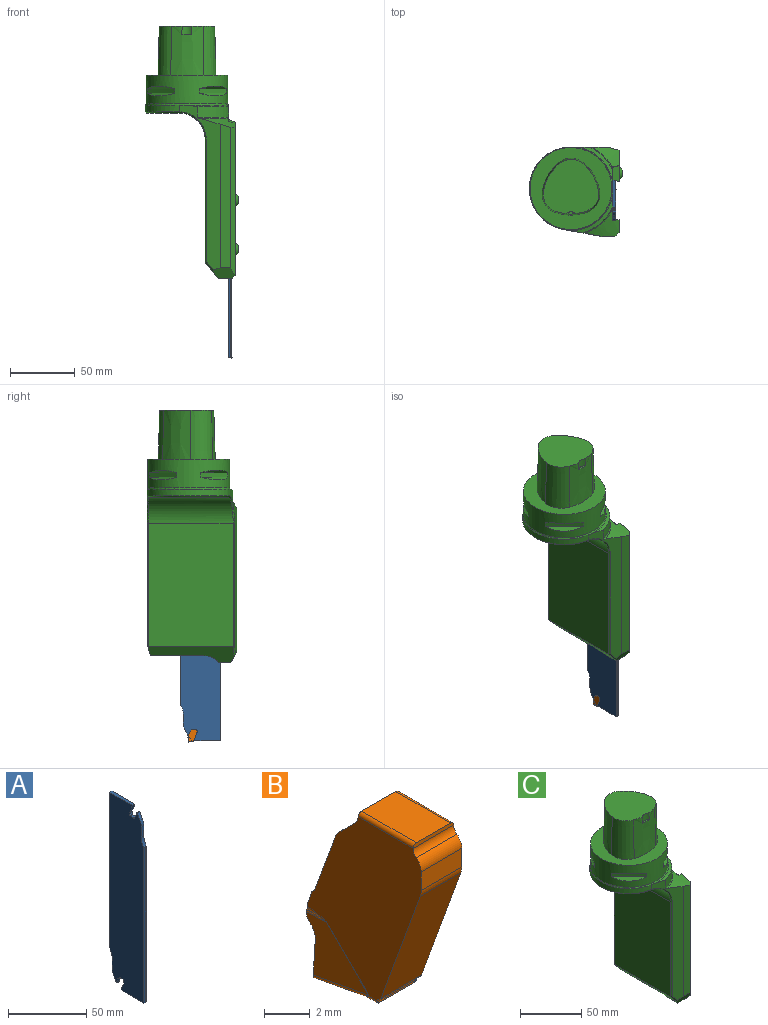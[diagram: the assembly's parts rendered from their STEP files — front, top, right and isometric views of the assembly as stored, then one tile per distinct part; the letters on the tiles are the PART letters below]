
ASSEMBLY  parts=3 mates=3
PART A: 58 faces, bbox 7.9x35x152.9 mm
  f0: plane 149.15x30.64mm, normal (-1,0,0), area 4314.1mm2, adj f1,f11,f12,f13,f14,f15,f16,f17
  f1: plane 2.35x0.99mm, normal (0,-1,0), area 2.3mm2, adj f0,f2,f11,f53
  f2: plane 149.15x30.64mm, normal (1,0,0), area 4314.1mm2, adj f1,f3,f4,f5,f7,f8,f9,f11
  f3: plane 121.39x1.19mm, normal (0.26,0.97,0), area 147.4mm2, adj f2,f49,f50,f51
  f4: cylinder r=0.2mm len=0.91mm, axis (-1,0,0), area 0mm2, adj f2,f41,f46
  f5: cylinder r=0.2mm len=3.37mm, axis (0,-1,0), area 0.5mm2, adj f2,f6,f34,f36
  f6: plane 3.37x2.1mm, normal (0,0,-1), area 7.1mm2, adj f5,f34,f35,f36
  f7: plane 121.39x1.19mm, normal (0.26,-0.97,0), area 147.4mm2, adj f2,f26,f27,f28
  f8: cylinder r=0.2mm len=0.91mm, axis (-1,0,0), area 0mm2, adj f2,f20,f23
  f9: cylinder r=0.2mm len=3.37mm, axis (0,1,0), area 0.5mm2, adj f2,f10,f13,f15
  f10: plane 3.37x2.1mm, normal (0,0,1), area 7.1mm2, adj f9,f13,f14,f15
  f11: cylinder r=0.75mm len=2.35mm, axis (-1,0,0), area 1.6mm2, adj f0,f1,f2,f12
  f12: cylinder r=0.5mm len=2.35mm, axis (-1,0,0), area 1.1mm2, adj f0,f2,f11,f13
  f13: plane 2.35x0.2mm, normal (0,-1,0), area 0.5mm2, adj f0,f2,f9,f10,f12,f14
  f14: cylinder r=0.2mm len=3.37mm, axis (0,-1,0), area 0.5mm2, adj f0,f10,f13,f15
  f15: plane 2.35x0.1mm, normal (0,1,0), area 0.2mm2, adj f0,f2,f9,f10,f14,f16
  f16: cylinder r=0.8mm len=2.35mm, axis (1,0,0), area 1.5mm2, adj f0,f2,f15,f17
  f17: plane 2.35x0.96mm, normal (0,0.71,0.71), area 3.2mm2, adj f0,f2,f16,f18
  f18: cylinder r=1mm len=2.35mm, axis (-1,0,0), area 1mm2, adj f0,f2,f17,f19
  f19: plane 3.38x2.35mm, normal (0,0.94,0.34), area 8.5mm2, adj f0,f2,f18,f20
  f20: cylinder r=0.4mm len=2.35mm, axis (-1,0,0), area 0.5mm2, adj f0,f2,f8,f19,f21,f22
  f21: bspline ~0.53x0.1mm, area 0mm2, adj f20,f23
  f22: cylinder r=0.2mm len=0.91mm, axis (-1,0,0), area 0mm2, adj f0,f20,f23
  f23: plane 4.37x2.56mm, normal (0,-0.87,0.5), area 11.6mm2, adj f0,f2,f8,f21,f22,f24
  f24: cylinder r=10mm len=5mm, axis (1,0,0), area 12.3mm2, adj f0,f2,f23,f25
  f25: plane 7.69x2.35mm, normal (0,-1,0), area 18.1mm2, adj f0,f2,f24,f26
  f26: cylinder r=13mm len=7.68mm, axis (-1,0,0), area 18.7mm2, adj f0,f2,f7,f25,f27
  f27: plane 121.39x1.19mm, normal (-0.26,-0.97,0), area 147.4mm2, adj f0,f7,f26,f28
  f28: plane 20.75x2.35mm, normal (0,0,-1), area 48.4mm2, adj f0,f2,f7,f27,f29
  f29: plane 6.61x2.41mm, normal (0,0.94,0.34), area 16.5mm2, adj f0,f2,f28,f30
  f30: cylinder r=1mm len=2.35mm, axis (1,0,0), area 0.8mm2, adj f0,f2,f29,f31
  f31: plane 2.35x0.99mm, normal (0,1,0), area 2.3mm2, adj f0,f2,f30,f32
  f32: cylinder r=0.75mm len=2.35mm, axis (-1,0,0), area 1.6mm2, adj f0,f2,f31,f33
  f33: cylinder r=0.5mm len=2.35mm, axis (-1,0,0), area 1.1mm2, adj f0,f2,f32,f34
  f34: plane 2.35x0.2mm, normal (0,1,0), area 0.5mm2, adj f0,f2,f5,f6,f33,f35
  f35: cylinder r=0.2mm len=3.37mm, axis (0,1,0), area 0.5mm2, adj f0,f6,f34,f36
  f36: plane 2.35x0.1mm, normal (0,-1,0), area 0.2mm2, adj f0,f2,f5,f6,f35,f37
  f37: cylinder r=0.8mm len=2.35mm, axis (1,0,0), area 1.5mm2, adj f0,f2,f36,f38
  f38: plane 2.35x0.96mm, normal (0,-0.71,-0.71), area 3.2mm2, adj f0,f2,f37,f39
  f39: cylinder r=1mm len=2.35mm, axis (-1,0,0), area 1mm2, adj f0,f2,f38,f40
  f40: plane 3.38x2.35mm, normal (0,-0.94,-0.34), area 8.5mm2, adj f0,f2,f39,f41
  f41: cylinder r=0.4mm len=2.35mm, axis (-1,0,0), area 0.5mm2, adj f0,f2,f4,f40,f42,f45
  f42: bspline ~0.53x0.1mm, area 0mm2, adj f41,f43,f44,f46
  f43: plane 5.57x3.98mm, normal (0,0.87,-0.5), area -0.2mm2, adj f42
  f44: plane 6x3.91mm, normal (0,0.87,-0.5), area 0.4mm2, adj f42
  f45: cylinder r=0.2mm len=0.91mm, axis (-1,0,0), area 0mm2, adj f0,f41,f46
  f46: plane 4.82x3.01mm, normal (0,0.87,-0.5), area 11.6mm2, adj f0,f2,f4,f42,f45,f47
  f47: cylinder r=10mm len=5mm, axis (1,0,0), area 12.3mm2, adj f0,f2,f46,f48
  f48: plane 7.69x2.35mm, normal (0,1,0), area 18.1mm2, adj f0,f2,f47,f49
  f49: cylinder r=13mm len=7.68mm, axis (-1,0,0), area 18.7mm2, adj f0,f2,f3,f48,f50
  f50: plane 121.39x1.19mm, normal (-0.26,0.97,0), area 147.4mm2, adj f0,f3,f49,f51
  f51: plane 20.75x2.35mm, normal (0,0,1), area 48.4mm2, adj f0,f2,f3,f50,f52
  f52: plane 6.61x2.41mm, normal (0,-0.94,-0.34), area 16.5mm2, adj f0,f2,f51,f53
  f53: cylinder r=1mm len=2.35mm, axis (1,0,0), area 0.8mm2, adj f0,f1,f2,f52
  f54: bspline ~0.53x0.1mm, area 0mm2, adj f55
  f55: sphere r=0.2mm, area 0.3mm2, adj f54
  f56: bspline ~0.53x0.1mm, area 0mm2, adj f57
  f57: sphere r=0.2mm, area 0mm2, adj f56
PART B: 78 faces, bbox 3x7x10 mm
  f0: plane 9.25x7mm, normal (1,0,0), area 40.2mm2, adj f3,f14,f17,f19,f20,f21,f30,f31
  f1: plane 9.25x7mm, normal (-1,0,0), area 40.2mm2, adj f4,f15,f18,f27,f28,f29,f30,f31
  f2: plane 3.37x2.1mm, normal (0,0,1), area 7.1mm2, adj f3,f4,f38,f57
  f3: cylinder r=0.2mm len=3.38mm, axis (0,-1,0), area 1.1mm2, adj f0,f2,f38,f49,f57
  f4: cylinder r=0.2mm len=3.38mm, axis (0,1,0), area 1.1mm2, adj f1,f2,f38,f49,f57
  f5: plane 3.77x3.02mm, normal (-1,-0.07,0.07), area 5.8mm2, adj f9,f13,f28,f58,f59,f60,f61
  f6: plane 0.41x0.06mm, normal (-0.86,-0.07,0.5), area 0mm2, adj f13,f15,f51
  f7: plane 3.77x3.02mm, normal (1,-0.07,0.07), area 5.8mm2, adj f10,f12,f20,f55,f56,f58,f61
  f8: plane 0.41x0.06mm, normal (0.86,-0.07,0.5), area 0mm2, adj f12,f14,f50
  f9: cylinder r=0.2mm len=3.2mm, axis (0.08,-0.99,0.12), area 1mm2, adj f5,f11,f26,f27,f61
  f10: cylinder r=0.2mm len=3.18mm, axis (-0.08,-0.99,0.12), area 1mm2, adj f7,f11,f21,f22,f61
  f11: plane 2.85x2.6mm, normal (0,-0.12,-0.99), area 6.8mm2, adj f9,f10,f23,f24,f25,f61
  f12: cylinder r=0.2mm len=1.18mm, axis (-0.07,-1,-0.02), area 0.1mm2, adj f7,f8,f19,f50,f56
  f13: cylinder r=0.2mm len=1.18mm, axis (0.07,-1,-0.02), area 0.1mm2, adj f5,f6,f29,f51,f60
  f14: cylinder r=0.2mm len=0.44mm, axis (0,0.99,0.14), area 0mm2, adj f0,f8,f19,f50
  f15: cylinder r=0.2mm len=0.44mm, axis (0,-0.99,-0.14), area 0mm2, adj f1,f6,f29,f51
  f16: plane 2.1x0.78mm, normal (0,0,-1), area 1.6mm2, adj f17,f18,f24,f39
  f17: cylinder r=0.2mm len=0.8mm, axis (0,1,0), area 0.2mm2, adj f0,f16,f22,f23,f37,f39
  f18: cylinder r=0.2mm len=0.8mm, axis (0,-1,0), area 0.2mm2, adj f1,f16,f25,f26,f37,f39
  f19: bspline ~0.78x0.2mm, area 0.1mm2, adj f0,f12,f14,f20
  f20: cylinder r=0.2mm len=2.6mm, axis (0,0.71,0.71), area 0.1mm2, adj f0,f7,f19,f21
  f21: plane 0.1x0.08mm, normal (1,-0.04,-0.01), area 0mm2, adj f0,f10,f20,f22
  f22: bspline ~0.32x0.22mm, area 0mm2, adj f10,f17,f21,f23
  f23: bspline ~0.03x0.03mm, area 0mm2, adj f11,f17,f22,f24
  f24: cylinder r=0.2mm len=2.1mm, axis (1,0,0), area 0.1mm2, adj f11,f16,f23,f25
  f25: cylinder r=0.13mm len=0.04mm, axis (-0.98,0.18,0.01), area 0mm2, adj f11,f18,f24,f26
  f26: bspline ~0.32x0.22mm, area 0mm2, adj f9,f18,f25,f27
  f27: plane 0.07x0.05mm, normal (-1,-0.04,-0.01), area 0mm2, adj f1,f9,f26,f28
  f28: cylinder r=0.2mm len=2.6mm, axis (0,-0.71,-0.71), area 0.1mm2, adj f1,f5,f27,f29
  f29: bspline ~0.78x0.2mm, area 0.1mm2, adj f1,f13,f15,f28
  f30: cylinder r=0.75mm len=2.5mm, axis (-1,0,0), area 1.7mm2, adj f0,f1,f31,f32
  f31: plane 2.5x0.99mm, normal (0,-1,0), area 2.5mm2, adj f0,f1,f30,f35
  f32: cylinder r=0.5mm len=2.5mm, axis (-1,0,0), area 1.2mm2, adj f0,f1,f30,f38
  f33: plane 6.66x2.5mm, normal (0,-0.94,-0.34), area 17.7mm2, adj f0,f1,f35,f36
  f34: plane 2.5x0.08mm, normal (0,-0.5,-0.87), area 0.2mm2, adj f0,f1,f36,f37
  f35: cylinder r=1mm len=2.5mm, axis (1,0,0), area 0.9mm2, adj f0,f1,f31,f33
  f36: cylinder r=0.1mm len=2.5mm, axis (-1,0,0), area 0.2mm2, adj f0,f1,f33,f34
  f37: cylinder r=0.3mm len=2.5mm, axis (-1,0,0), area 0.8mm2, adj f0,f1,f17,f18,f34,f39
  f38: plane 2.5x0.2mm, normal (0,-1,0), area 0.5mm2, adj f2,f3,f4,f32
  f39: plane 2.45x0.1mm, normal (0,-1,0), area 0.2mm2, adj f16,f17,f18,f37
  f40: cylinder r=0.2mm len=0.99mm, axis (-1,0,0), area 0.1mm2, adj f0,f42,f44,f77
  f41: cylinder r=0.2mm len=0.66mm, axis (1,0,0), area 0mm2, adj f0,f42,f50,f73
  f42: plane 0.99x0.69mm, normal (0,0.94,0.34), area 0.6mm2, adj f0,f40,f41,f75
  f43: cylinder r=0.2mm len=1.01mm, axis (-1,0,0), area 0.1mm2, adj f1,f44,f48,f74,f76
  f44: cylinder r=0.4mm len=2.5mm, axis (-1,0,0), area 0.6mm2, adj f0,f1,f40,f43,f45,f76
  f45: plane 3.38x2.5mm, normal (0,0.94,0.34), area 9mm2, adj f0,f1,f44,f47
  f46: plane 2.5x0.96mm, normal (0,0.71,0.71), area 3.4mm2, adj f0,f1,f47,f49
  f47: cylinder r=1mm len=2.5mm, axis (-1,0,0), area 1.1mm2, adj f0,f1,f45,f46
  f48: plane 0.99x0.72mm, normal (0,0.94,0.34), area 0.6mm2, adj f1,f43,f51,f74
  f49: cylinder r=0.8mm len=2.5mm, axis (1,0,0), area 1.6mm2, adj f0,f1,f3,f4,f46,f57
  f50: plane 0.74x0.37mm, normal (0,1,0), area 0.2mm2, adj f0,f8,f12,f14,f41,f56,f69,f71
  f51: plane 0.74x0.41mm, normal (0,1,0), area 0.3mm2, adj f1,f6,f13,f15,f48,f60,f70,f72
  f52: cylinder r=0.45mm len=1.99mm, axis (0,0.12,0.99), area 1.5mm2, adj f53,f54,f62,f63,f64,f65,f66,f71
  f53: plane 0.38x0.05mm, normal (-0.93,0.37,-0.05), area 0mm2, adj f52,f67,f69
  f54: plane 0.38x0.05mm, normal (0.93,0.37,-0.05), area 0mm2, adj f52,f68,f70
  f55: plane 0.85x0.16mm, normal (0,0.71,-0.71), area 0.2mm2, adj f7,f56,f58,f63
  f56: cylinder r=0.5mm len=0.76mm, axis (-1,0,0), area 0.3mm2, adj f7,f12,f50,f55,f65,f67
  f57: plane 2.45x0.1mm, normal (0,1,0), area 0.2mm2, adj f2,f3,f4,f49
  f58: cylinder r=1mm len=2.75mm, axis (-1,0,0), area 1.8mm2, adj f5,f7,f55,f59,f61,f62
  f59: plane 0.85x0.16mm, normal (0,0.71,-0.71), area 0.2mm2, adj f5,f58,f60,f64
  f60: cylinder r=0.5mm len=0.76mm, axis (-1,0,0), area 0.3mm2, adj f5,f13,f51,f59,f66,f68
  f61: plane 3.02x2.02mm, normal (0,1,0), area 5.8mm2, adj f5,f7,f9,f10,f11,f58
  f62: bspline ~1x0.52mm, area 0.2mm2, adj f52,f58,f63,f64
  f63: bspline ~0.29x0.24mm, area 0.1mm2, adj f52,f55,f62,f65
  f64: bspline ~0.29x0.24mm, area 0.1mm2, adj f52,f59,f62,f66
  f65: bspline ~0.2x0.18mm, area 0mm2, adj f52,f56,f63,f67
  f66: bspline ~0.2x0.18mm, area 0mm2, adj f52,f60,f64,f68
  f67: bspline ~0.27x0.2mm, area 0.1mm2, adj f53,f56,f65,f69
  f68: bspline ~0.27x0.2mm, area 0.1mm2, adj f54,f60,f66,f70
  f69: cylinder r=0.2mm len=0.23mm, axis (0.05,0,-1), area 0.1mm2, adj f50,f53,f67,f71
  f70: cylinder r=0.2mm len=0.23mm, axis (0.05,0,1), area 0.1mm2, adj f51,f54,f68,f72
  f71: cylinder r=0.2mm len=0.19mm, axis (-0.05,0,1), area 0mm2, adj f50,f52,f69,f73
  f72: cylinder r=0.2mm len=0.2mm, axis (0.06,0,1), area 0mm2, adj f51,f52,f70,f74
  f73: sphere r=0.2mm, area 0mm2, adj f41,f71,f75
  f74: bspline ~0.81x0.43mm, area 0.1mm2, adj f43,f48,f51,f52,f72,f76
  f75: bspline ~0.77x0.41mm, area 0.1mm2, adj f42,f52,f73,f77
  f76: bspline ~0.56x0.23mm, area 0.1mm2, adj f43,f44,f52,f74,f77
  f77: sphere r=0.2mm, area 0mm2, adj f40,f75,f76
PART C: 103 faces, bbox 80.9x91.1x194.7 mm
  f0: plane 3.16x0.1mm, normal (-1,0,0), area 0.3mm2, adj f1,f19,f41,f102
  f1: plane 3.51x0.7mm, normal (0,0,-1), area 2.4mm2, adj f0,f3,f41,f102
  f2: plane 3.16x0.1mm, normal (1,0,0), area 0.3mm2, adj f19,f40,f42,f102
  f3: plane 3.16x0.1mm, normal (1,0,0), area 0.3mm2, adj f1,f19,f41,f102
  f4: plane 76.42x8.84mm, normal (1,0,0), area 666.9mm2, adj f19,f21,f23,f24
  f5: plane 117.48x10.61mm, normal (1,0,0), area 1151.5mm2, adj f10,f22,f27,f36,f37
  f6: plane 133.26x39.63mm, normal (1,0,0), area 4060.6mm2, adj f10,f11,f12,f13,f14,f15,f16,f17
  f7: plane 114.13x11.55mm, normal (1,0,0), area 1288mm2, adj f11,f21,f23,f25,f43,f53
  f8: plane 10.93x9.38mm, normal (0,0,-1), area 97.4mm2, adj f20,f26,f27,f28,f32,f36,f37
  f9: plane 110.77x8.49mm, normal (0,-1,0), area 881.7mm2, adj f10,f22,f29,f36
  f10: cone r=35mm half-angle=65deg, axis (0,0,-1), area 269.8mm2, adj f5,f6,f9,f17,f22,f26,f27,f28
  f11: cone r=35mm half-angle=65deg, axis (0,0,-1), area 181.3mm2, adj f6,f7,f18,f25,f30,f38,f43
  f12: cone r=50mm half-angle=75deg, axis (0,0,-1), area 106.5mm2, adj f6,f14,f15,f29
  f13: cone r=50mm half-angle=75deg, axis (0,0,-1), area 90.6mm2, adj f6,f14,f16,f30
  f14: torus R=32.7mm, axis (0,0,1), area 267.6mm2, adj f6,f12,f13,f29,f30,f31,f54
  f15: cylinder r=35mm len=23.59mm, axis (0,0,1), area 267.2mm2, adj f6,f12,f17,f29
  f16: cylinder r=35mm len=17.82mm, axis (0,0,1), area 216mm2, adj f6,f13,f18,f30
  f17: torus R=36.2mm, axis (0,0,1), area 41.7mm2, adj f6,f10,f15,f29
  f18: torus R=36.2mm, axis (0,0,1), area 33.3mm2, adj f6,f11,f16,f30
  f19: plane 40.97x16.13mm, normal (0,0,-1), area 446.2mm2, adj f0,f2,f3,f4,f6,f20,f23,f24
  f20: cylinder r=16mm len=12.13mm, axis (1,0,0), area 139.1mm2, adj f6,f8,f19,f26,f32
  f21: cone r=6.94mm half-angle=15deg, axis (1,0,0), area 80mm2, adj f4,f6,f7,f23,f24,f25,f38
  f22: cylinder r=50mm len=113.84mm, axis (0,0,1), area 528.8mm2, adj f5,f9,f10,f36
  f23: plane 72x9.4mm, normal (0.26,-0.97,0), area 209.9mm2, adj f4,f7,f19,f21,f53,f80,f81,f84
  f24: plane 72x4.4mm, normal (0.26,0.97,0), area 328mm2, adj f4,f6,f19,f21
  f25: plane 43.93x4.76mm, normal (0.26,-0.97,0), area 207.8mm2, adj f7,f11,f21,f38
  f26: plane 121.07x1.29mm, normal (0.97,-0.26,0), area 160.1mm2, adj f6,f8,f10,f20,f28
  f27: plane 120.34x4.51mm, normal (-0.26,0.97,0), area 537.8mm2, adj f5,f8,f10,f28,f37
  f28: cylinder r=0.8mm len=120.84mm, axis (0,0,1), area 201.9mm2, adj f8,f10,f26,f27
  f29: plane 127.32x31.78mm, normal (-0.17,-0.98,0), area 1341.9mm2, adj f9,f10,f12,f14,f15,f17,f31,f36
  f30: plane 119.7x28.67mm, normal (0,1,0), area 1550.1mm2, adj f11,f13,f14,f16,f18,f31,f43,f46
  f31: cylinder r=32mm len=63.51mm, axis (0,0,1), area 479.9mm2, adj f14,f29,f30,f47,f49,f50
  f32: plane 66.4x12mm, normal (-0.77,0,-0.64), area 687.9mm2, adj f8,f19,f20,f35,f36,f46,f51,f52
  f33: cylinder r=20mm len=65.12mm, axis (0,1,0), area 2001.9mm2, adj f34,f35,f45,f47,f48,f50
  f34: plane 60.83x25mm, normal (0,0,-1), area 1139.9mm2, adj f33,f49
  f35: plane 95x65.12mm, normal (-1,0,0), area 6186.7mm2, adj f32,f33,f44,f46,f51
  f36: plane 16.95x8.14mm, normal (0,-0.87,-0.5), area 126.5mm2, adj f5,f8,f9,f22,f29,f32,f37,f51
  f37: plane 9.88x2mm, normal (0.71,0,-0.71), area 25.5mm2, adj f5,f8,f27,f36
  f38: cylinder r=0.4mm len=44.07mm, axis (0,0,-1), area 22.8mm2, adj f6,f11,f21,f25
  f39: plane 3.16x0.1mm, normal (-1,0,0), area 0.3mm2, adj f19,f40,f42,f102
  f40: plane 3.51x0.7mm, normal (0,0,-1), area 2.4mm2, adj f2,f39,f42,f102
  f41: cylinder r=0.35mm len=0.7mm, axis (0,0,-1), area 0.1mm2, adj f0,f1,f3,f19
  f42: cylinder r=0.35mm len=0.7mm, axis (0,0,-1), area 0.1mm2, adj f2,f19,f39,f40
  f43: plane 113.99x9mm, normal (0.26,0.97,0), area 1014.6mm2, adj f7,f11,f30,f52,f53
  f44: plane 94.7x0.99mm, normal (-0.77,-0.64,0), area 121.4mm2, adj f29,f35,f45,f51
  f45: bspline ~20.99x20.38mm, area 42.4mm2, adj f29,f33,f44,f47
  f46: plane 95.42x1mm, normal (-0.71,0.71,0), area 133.7mm2, adj f30,f32,f35,f48,f52
  f47: bspline ~1.1x1.01mm, area 0.9mm2, adj f31,f33,f45,f49
  f48: cone r=20mm half-angle=45deg, axis (0,1,0), area 37.1mm2, adj f30,f33,f46,f50
  f49: cone r=31mm half-angle=45deg, axis (0,0,1), area 122.6mm2, adj f31,f34,f47,f50
  f50: bspline ~6.19x1.83mm, area 8.6mm2, adj f31,f33,f48,f49
  f51: plane 8.19x6.23mm, normal (-0.59,-0.7,-0.39), area 15mm2, adj f29,f32,f35,f36,f44
  f52: plane 22.15x9mm, normal (0,0.97,-0.26), area 149.2mm2, adj f19,f30,f32,f43,f46,f53
  f53: plane 11.75x1mm, normal (0.71,0,-0.71), area 16.3mm2, adj f7,f19,f23,f43,f52
  f54: cylinder r=31.5mm len=63mm, axis (0,0,-1), area 3588.8mm2, adj f14,f62,f65,f66,f67,f68,f69,f70
  f55: cone r=36mm half-angle=1.4deg, axis (0,0,-1), area 960.3mm2, adj f56,f60,f61,f62
  f56: cone r=15mm half-angle=1.4deg, axis (0,0,-1), area 761.8mm2, adj f55,f57,f61,f62
  f57: cone r=36mm half-angle=1.4deg, axis (0,0,-1), area 945mm2, adj f56,f58,f61,f62
  f58: cone r=15mm half-angle=1.4deg, axis (0,0,-1), area 761.8mm2, adj f57,f59,f61,f62
  f59: cone r=36mm half-angle=1.4deg, axis (0,0,-1), area 911mm2, adj f58,f60,f61,f62,f63,f64
  f60: cone r=15mm half-angle=1.4deg, axis (0,0,-1), area 773.3mm2, adj f55,f59,f61,f62
  f61: plane 42.71x41.75mm, normal (0,0,1), area 1367.8mm2, adj f55,f56,f57,f58,f59,f60,f64
  f62: plane 63x63mm, normal (0,0,1), area 1612.2mm2, adj f54,f55,f56,f57,f58,f59,f60
  f63: plane 7.8x1.66mm, normal (0,0,1), area 8.8mm2, adj f59,f64
  f64: cylinder r=6mm len=7.8mm, axis (0,0,-1), area 53.3mm2, adj f59,f61,f63
  f65: plane 20.73x20.73mm, normal (-0.35,-0.35,-0.87), area 82.7mm2, adj f54,f66
  f66: plane 20.73x20.73mm, normal (-0.71,-0.71,0), area 102.6mm2, adj f54,f65,f67
  f67: plane 20.73x20.73mm, normal (-0.35,-0.35,0.87), area 82.7mm2, adj f54,f66
  f68: plane 20.73x20.73mm, normal (-0.35,0.35,-0.87), area 82.7mm2, adj f54,f69
  f69: plane 20.73x20.73mm, normal (-0.71,0.71,0), area 102.6mm2, adj f54,f68,f70
  f70: plane 20.73x20.73mm, normal (-0.35,0.35,0.87), area 82.7mm2, adj f54,f69
  f71: plane 20.73x20.73mm, normal (0.35,0.35,-0.87), area 82.7mm2, adj f54,f72
  f72: plane 20.73x20.73mm, normal (0.71,0.71,0), area 102.6mm2, adj f54,f71,f73
  f73: plane 20.73x20.73mm, normal (0.35,0.35,0.87), area 82.7mm2, adj f54,f72
  f74: plane 20.73x20.73mm, normal (0.35,-0.35,-0.87), area 82.7mm2, adj f54,f75
  f75: plane 20.73x20.73mm, normal (0.71,-0.71,0), area 102.6mm2, adj f54,f74,f76
  f76: plane 20.73x20.73mm, normal (0.35,-0.35,0.87), area 82.7mm2, adj f54,f75
  f77: plane 34x12.35mm, normal (1,0,0), area 348.7mm2, adj f78,f81,f82,f83,f84,f85,f87
  f78: plane 34x0.6mm, normal (0,-1,0), area 20.4mm2, adj f77,f79,f82,f83
  f79: plane 34x7.4mm, normal (-0.26,-0.97,0), area 260.5mm2, adj f78,f80,f82,f83
  f80: plane 34x8.38mm, normal (-1,0,0), area 284.5mm2, adj f23,f79,f82,f83,f84,f85
  f81: plane 32.54x0.6mm, normal (0,1,0), area 19.4mm2, adj f23,f77,f84,f85
  f82: plane 11.91x8mm, normal (0,0,1), area 79.4mm2, adj f77,f78,f79,f80,f84
  f83: plane 11.91x8mm, normal (0,0,-1), area 79.4mm2, adj f77,f78,f79,f80,f85
  f84: plane 8x2.58mm, normal (-0.22,0.84,0.5), area 9.5mm2, adj f23,f77,f80,f81,f82
  f85: plane 8x2.58mm, normal (-0.22,0.84,-0.5), area 9.5mm2, adj f23,f77,f80,f81,f83
  f86: plane 5x5mm, normal (1,0,0), area 19.6mm2, adj f88
  f87: cylinder r=4.75mm len=9.5mm, axis (-1,0,0), area 14.9mm2, adj f77,f88
  f88: torus R=0.27mm, axis (-1,0,0), area 76.2mm2, adj f86,f87
  f89: plane 34x12.35mm, normal (1,0,0), area 348.7mm2, adj f90,f93,f94,f95,f96,f97,f99
  f90: plane 34x0.6mm, normal (0,-1,0), area 20.4mm2, adj f89,f91,f94,f95
  f91: plane 34x7.4mm, normal (-0.26,-0.97,0), area 260.5mm2, adj f90,f92,f94,f95
  f92: plane 34x8.38mm, normal (-1,0,0), area 284.5mm2, adj f23,f91,f94,f95,f96,f97
  f93: plane 32.54x0.6mm, normal (0,1,0), area 19.4mm2, adj f23,f89,f96,f97
  f94: plane 11.91x8mm, normal (0,0,1), area 79.4mm2, adj f89,f90,f91,f92,f96
  f95: plane 11.91x8mm, normal (0,0,-1), area 79.4mm2, adj f89,f90,f91,f92,f97
  f96: plane 8x2.58mm, normal (-0.22,0.84,0.5), area 9.5mm2, adj f23,f89,f92,f93,f94
  f97: plane 8x2.58mm, normal (-0.22,0.84,-0.5), area 9.5mm2, adj f23,f89,f92,f93,f95
  f98: plane 5x5mm, normal (1,0,0), area 19.6mm2, adj f100
  f99: cylinder r=4.75mm len=9.5mm, axis (-1,0,0), area 14.9mm2, adj f89,f100
  f100: torus R=0.27mm, axis (-1,0,0), area 76.2mm2, adj f98,f99
  f101: plane 8.01x8.01mm, normal (0,0,-1), area 50.4mm2, adj f102
  f102: cylinder r=4.01mm len=8.01mm, axis (0,0,1), area 5.7mm2, adj f0,f1,f2,f3,f19,f39,f40,f101
PLACE A t=(34.35,-25,-67.44)mm
PLACE B t=(34.35,-25,-67.44)mm
PLACE C at identity
MATE fastened B.f2 <-> A.f6  axis (0,0,1) through (33.17,-4.21,-207.44)mm
MATE planar A.f7 <-> C.f27  axis (0.26,-0.97,0) through (33.76,-24.53,-156.02)mm
MATE planar A.f0 <-> C.f6  axis (-1,0,0) through (32,-9.05,-142.02)mm
